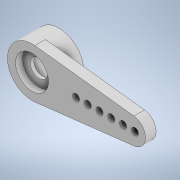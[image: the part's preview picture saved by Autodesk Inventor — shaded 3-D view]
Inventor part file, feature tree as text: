
AUTODESK INVENTOR PART (.ipt)
format: ipt  version: 2020 (Build 240168000, 168)  size: 154,624 bytes
history: native  units: mm
features: extrude x4, sketch x4
ambient origin geometry x8: Origin, YZ Plane, XZ Plane, XY Plane, X Axis, Y Axis, Z Axis, Center Point
bodies: Solid1 (feature_tree)
feature tree (8):
  extrude  "Extrusion1"  Depth=1.85mm
  extrude  "Extrusion2"  Depth=1.0mm
  extrude  "Extrusion3"  Depth=1.5mm
  extrude  "Extrusion4"  Depth=0.5mm
  sketch  "Sketch1"  dims[d1=19.55mm d2=1.85mm]
  sketch  "Sketch2"  dims[d3=6.97mm d4=1.0mm]
  sketch  "Sketch3"  dims[d5=60.0mm d7=1.666667mm d8=10.0mm d10=10.0mm d12=1.5mm]
  sketch  "Sketch4"  dims[d13=1.5mm d14=0.0mm d15=4.67mm d16=2.5mm d17=1.5mm d18=0.0mm d19=2.33mm d20=0.0mm d21=2.5mm d22=0.5mm d23=0.0mm]
